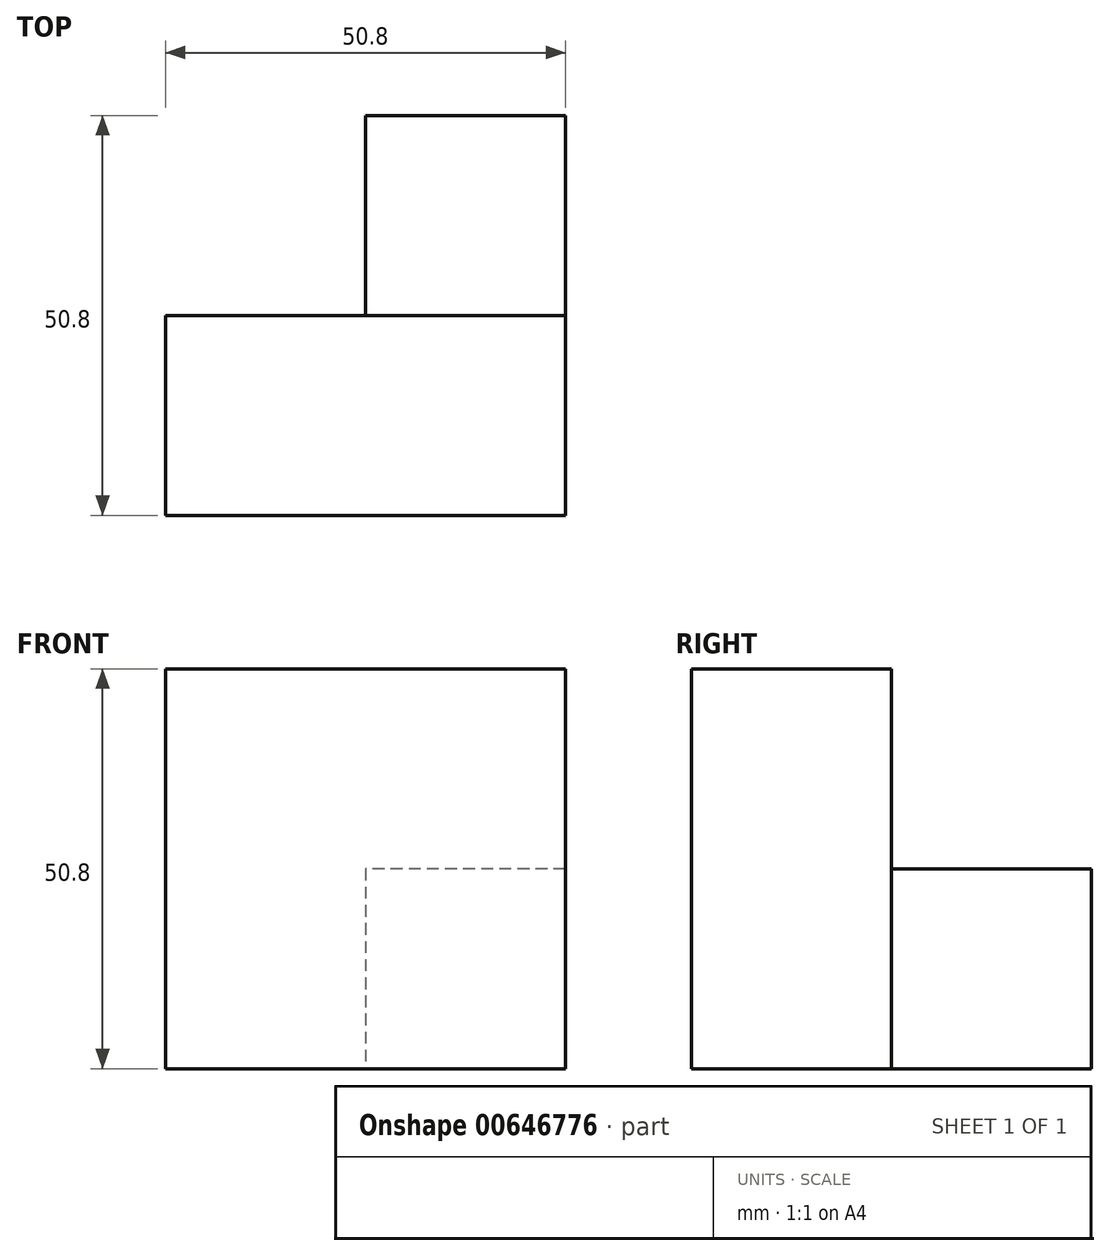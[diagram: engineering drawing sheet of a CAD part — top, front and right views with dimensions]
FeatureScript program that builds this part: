
annotation { "Feature Type Name" : "Feature", "Feature Type Description" : "" }
export const myFeature = defineFeature(function(context is Context, id is Id, definition is map)
    precondition{}
    {
        {
            var Q0;
            Q0=qCreatedBy(makeId("Front.planeOp"),FACE);
            var sketch = newSketch(context, id + "F0", { "sketchPlane" : qUnion([Q0])});
            skLineSegment(sketch, "E0", {"start": v(-25.4, 25.4) * mm, "end": v(-25.4, 0) * mm});
            skLineSegment(sketch, "E1", {"start": v(-25.4, 0) * mm, "end": v(0, 0) * mm});
            skLineSegment(sketch, "E2", {"start": v(0, 0) * mm, "end": v(0, 25.4) * mm});
            skLineSegment(sketch, "E3", {"start": v(0, 25.4) * mm, "end": v(-25.4, 25.4) * mm});
            skSolve(sketch);
        }
        {
            var Q0;
            Q0=makeQuery(id+"F0.imprint","IMPRINT",FACE,{"disambiguationData":[TD([[makeQuery(id+"F0.imprint","IMPRINT",EDGE,{"derivedFrom":sQuery(id+"F0.wireOp",EDGE,"E0")}),1.0]])]});
            extrude(context, id + "F1", {"entities" : qUnion([Q0]), "depth" : 25.4 * mm, "offsetDistance" : 25.4 * mm});
        }
        {
            var Q0;
            Q0=makeQuery(id+"F1.opExtrude","CAP_FACE",FACE,{"disambiguationData":[OSD([sQuery(id+"F0.wireOp",EDGE,"E0"),sQuery(id+"F0.wireOp",EDGE,"E1"),sQuery(id+"F0.wireOp",EDGE,"E2"),sQuery(id+"F0.wireOp",EDGE,"E3")])],"isStart":false});
            var sketch = newSketch(context, id + "F2", { "sketchPlane" : qUnion([Q0])});
            skLineSegment(sketch, "E4", {"start": v(0, 0) * mm, "end": v(-50.8, 0) * mm});
            skLineSegment(sketch, "E5", {"start": v(-50.8, 0) * mm, "end": v(-50.8, 50.8) * mm});
            skLineSegment(sketch, "E6", {"start": v(-50.8, 50.8) * mm, "end": v(0, 50.8) * mm});
            skLineSegment(sketch, "E7", {"start": v(0, 50.8) * mm, "end": v(0, 0) * mm});
            skSolve(sketch);
        }
        {
            var Q0;
            Q0 = qSketchRegion(id + "F2", true);
            extrude(context, id + "F3", {"entities" : qUnion([Q0]), "depth" : 25.4 * mm, "offsetDistance" : 25.4 * mm});
        }
    });
